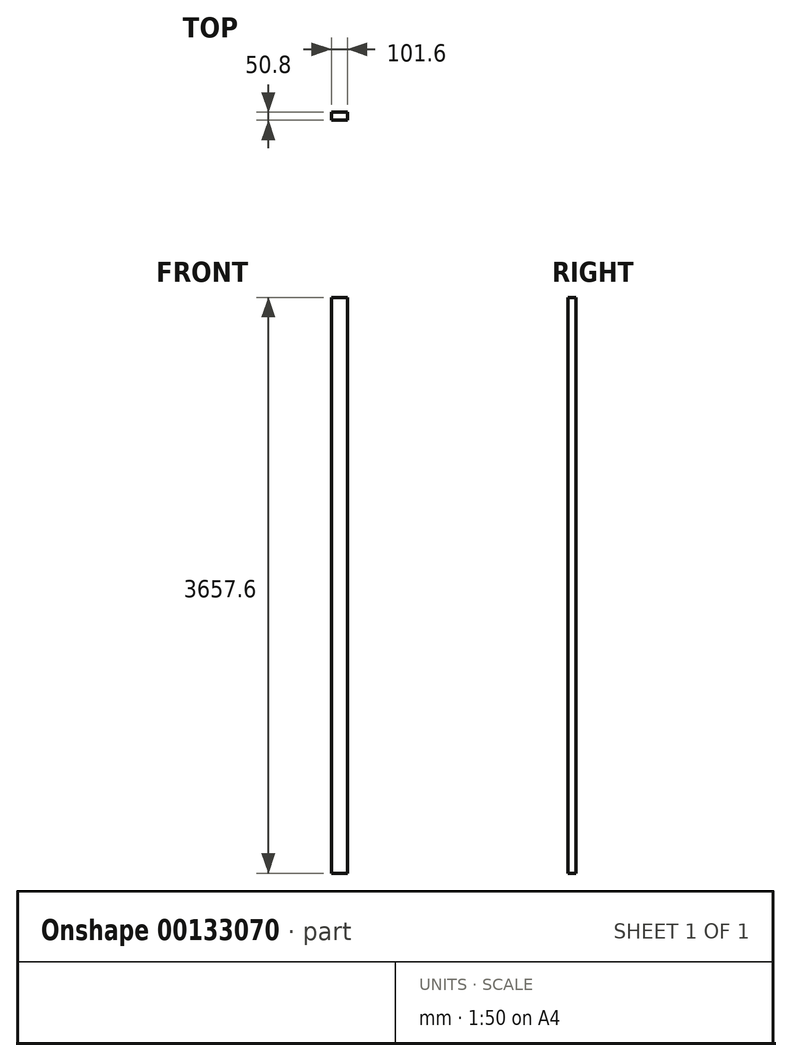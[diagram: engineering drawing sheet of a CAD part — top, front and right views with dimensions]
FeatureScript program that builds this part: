
annotation { "Feature Type Name" : "Feature", "Feature Type Description" : "" }
export const myFeature = defineFeature(function(context is Context, id is Id, definition is map)
    precondition{}
    {
        {
            var Q0;
            Q0=qCreatedBy(makeId("Front.planeOp"),FACE);
            var sketch = newSketch(context, id + "F0", { "sketchPlane" : qUnion([Q0])});
            skLineSegment(sketch, "E0", {"start": v(0, 0) * mm, "end": v(0, 3657.6) * mm});
            skLineSegment(sketch, "E1", {"start": v(0, 3657.6) * mm, "end": v(101.6, 3657.6) * mm});
            skLineSegment(sketch, "E2", {"start": v(101.6, 3657.6) * mm, "end": v(101.6, 0) * mm});
            skLineSegment(sketch, "E3", {"start": v(101.6, 0) * mm, "end": v(0, 0) * mm});
            skSolve(sketch);
        }
        {
            var Q0;
            Q0 = qSketchRegion(id + "F0", true);
            extrude(context, id + "F1", {"entities" : qUnion([Q0]), "depth" : 50.8 * mm});
        }
    });
